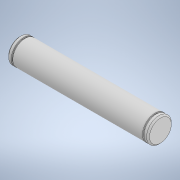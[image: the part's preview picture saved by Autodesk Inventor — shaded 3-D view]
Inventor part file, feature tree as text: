
AUTODESK INVENTOR PART (.ipt)
format: ipt  version: 2022 (Build 260153000, 153)  size: 126,464 bytes
history: native  units: mm
features: revolve x1, sketch x1
ambient origin geometry x8: Origin, YZ Plane, XZ Plane, XY Plane, X Axis, Y Axis, Z Axis, Center Point
bodies: Solid1 (feature_tree)
feature tree (2):
  revolve  "Revolution1"  [1 undecoded]
  sketch  "Sketch1"  dims[d0=6.0mm d1=0.7mm d2=2.0mm d3=0.5mm d4=135.0deg d5=1.0mm d7=90.0deg d8=31.5mm]
note: 1 required parameter value undecoded (feature->parameter linkage not recoverable at this tier; creation-order binding heuristic only, values carry confidence <= 0.55)
